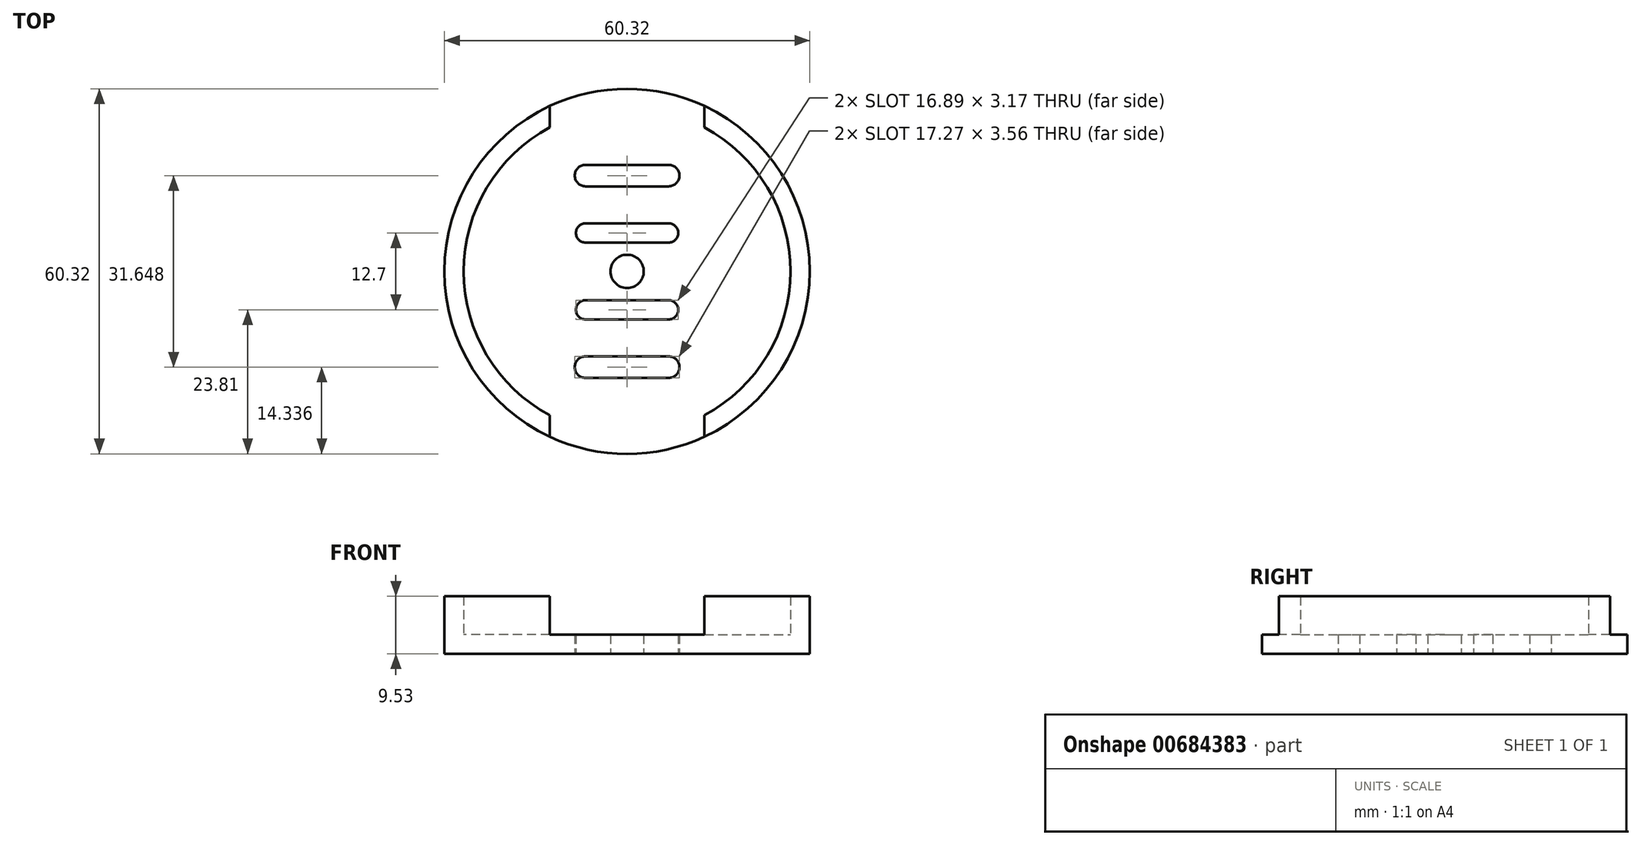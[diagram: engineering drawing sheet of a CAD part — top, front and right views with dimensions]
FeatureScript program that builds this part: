
annotation { "Feature Type Name" : "Feature", "Feature Type Description" : "" }
export const myFeature = defineFeature(function(context is Context, id is Id, definition is map)
    precondition{}
    {
        {
            var Q0;
            Q0=qCreatedBy(makeId("Top.planeOp"),FACE);
            var sketch = newSketch(context, id + "F0", { "sketchPlane" : qUnion([Q0])});
            skCircle(sketch, "E0", {"center": v(0, 0) * mm, "radius": 30.16 * mm});
            skSolve(sketch);
        }
        {
            var Q0;
            Q0=makeQuery(id+"F0.imprint","IMPRINT",FACE,{"disambiguationData":[TD([[makeQuery(id+"F0.imprint","IMPRINT",EDGE,{"derivedFrom":sQuery(id+"F0.wireOp",EDGE,"E0")}),1.0]])]});
            extrude(context, id + "F1", {"entities" : qUnion([Q0]), "depth" : 3.17 * mm, "offsetDistance" : 25.4 * mm});
        }
        {
            var Q0;
            Q0=makeQuery(id+"F1.opExtrude","CAP_FACE",FACE,{"disambiguationData":[OSD([sQuery(id+"F0.wireOp",EDGE,"E0")])],"isStart":false});
            var sketch = newSketch(context, id + "F2", { "sketchPlane" : qUnion([Q0])});
            skArc(sketch, "E1.0", {"start": v(-12.75, 23.79) * mm, "mid": v(-26.99, 0) * mm, "end": v(-12.75, -23.79) * mm});
            skLineSegment(sketch, "E2", {"start": v(-16.9, 36.23) * mm, "end": v(14.72, -31.57) * mm, "construction": true});
            skLineSegment(sketch, "E3", {"start": v(16.9, 36.23) * mm, "end": v(-14.08, -30.2) * mm, "construction": true});
            skLineSegment(sketch, "E4", {"start": v(-12.75, 27.34) * mm, "end": v(-12.75, 23.79) * mm});
            skLineSegment(sketch, "E5", {"start": v(12.75, 27.34) * mm, "end": v(12.75, 23.79) * mm});
            skLineSegment(sketch, "E6.trimOffspring", {"start": v(-12.75, -23.79) * mm, "end": v(-12.75, -27.34) * mm});
            skLineSegment(sketch, "E7.trimOffspring", {"start": v(12.75, -23.79) * mm, "end": v(12.75, -27.34) * mm});
            skArc(sketch, "E8.trimOffspring", {"start": v(12.75, -23.79) * mm, "mid": v(26.99, 0) * mm, "end": v(12.75, 23.79) * mm});
            skSolve(sketch);
        }
        {
            var Q0;
            Q0=makeQuery(id+"F2.imprint","IMPRINT",FACE,{"disambiguationData":[TD([[makeQuery(id+"F2.imprint","IMPRINT",EDGE,{"derivedFrom":sQuery(id+"F2.wireOp",EDGE,"E1.0")}),-1.0]])]});
            var Q1;
            {var subQ0=sQuery(id+"F2.wireOp",EDGE,"E5");Q1=makeQuery(id+"F2.imprint","IMPRINT",FACE,{"disambiguationData":[TD([[makeQuery(id+"F2.imprint","IMPRINT",EDGE,{"derivedFrom":subQ0}),1.0]])]});}
            extrude(context, id + "F3", {"entities" : qUnion([Q0, Q1]), "operationType" : NewBodyOperationType.ADD, "depth" : 6.35 * mm, "offsetDistance" : 25.4 * mm});
        }
        {
            var Q0;
            Q0=makeQuery(id+"F1.opExtrude","CAP_FACE",FACE,{"disambiguationData":[OSD([sQuery(id+"F0.wireOp",EDGE,"E0")])],"isStart":true});
            var sketch = newSketch(context, id + "F4", { "sketchPlane" : qUnion([Q0])});
            skPoint(sketch, "E9", {"position": v(-6.86, 15.82) * mm});
            skPoint(sketch, "E10.MirrorP", {"position": v(6.86, 15.82) * mm});
            skArc(sketch, "E11", {"start": v(-6.86, 17.6) * mm, "mid": v(-8.64, 15.82) * mm, "end": v(-6.86, 14.05) * mm});
            skArc(sketch, "E12.MirrorC", {"start": v(6.86, 17.6) * mm, "mid": v(8.64, 15.82) * mm, "end": v(6.86, 14.05) * mm});
            skLineSegment(sketch, "E13", {"start": v(-6.86, 17.6) * mm, "end": v(6.86, 17.6) * mm});
            skLineSegment(sketch, "E14", {"start": v(6.86, 14.05) * mm, "end": v(-6.86, 14.05) * mm});
            skLineSegment(sketch, "E15.MirrorCS", {"start": v(6.86, -14.05) * mm, "end": v(-6.86, -14.05) * mm});
            skLineSegment(sketch, "E16.MirrorCS", {"start": v(-6.86, -17.6) * mm, "end": v(6.86, -17.6) * mm});
            skArc(sketch, "E17.MirrorCS", {"start": v(6.86, -17.6) * mm, "mid": v(8.64, -15.82) * mm, "end": v(6.86, -14.05) * mm});
            skArc(sketch, "E18.MirrorCS", {"start": v(-6.86, -17.6) * mm, "mid": v(-8.64, -15.82) * mm, "end": v(-6.86, -14.05) * mm});
            skCircle(sketch, "E19", {"center": v(0, 0) * mm, "radius": 2.75 * mm});
            skCircle(sketch, "E20", {"center": v(-6.86, 6.35) * mm, "radius": 1.59 * mm});
            skCircle(sketch, "E21", {"center": v(6.86, 6.35) * mm, "radius": 1.59 * mm});
            skLineSegment(sketch, "E22", {"start": v(-6.86, 4.76) * mm, "end": v(6.86, 4.76) * mm});
            skLineSegment(sketch, "E23", {"start": v(-6.86, 7.94) * mm, "end": v(6.86, 7.94) * mm});
            skLineSegment(sketch, "E24.MirrorCS", {"start": v(-6.86, -4.76) * mm, "end": v(6.86, -4.76) * mm});
            skLineSegment(sketch, "E25.MirrorCS", {"start": v(-6.86, -7.94) * mm, "end": v(6.86, -7.94) * mm});
            skCircle(sketch, "E26.MirrorC", {"center": v(-6.86, -6.35) * mm, "radius": 1.59 * mm});
            skCircle(sketch, "E27.MirrorC", {"center": v(6.86, -6.35) * mm, "radius": 1.59 * mm});
            skSolve(sketch);
        }
        {
            var Q0;
            Q0 = qSketchRegion(id + "F4", true);
            extrude(context, id + "F5", {"entities" : qUnion([Q0]), "operationType" : NewBodyOperationType.REMOVE, "oppositeDirection" : true, "depth" : 25.4 * mm, "offsetDistance" : 25.4 * mm});
        }
    });
